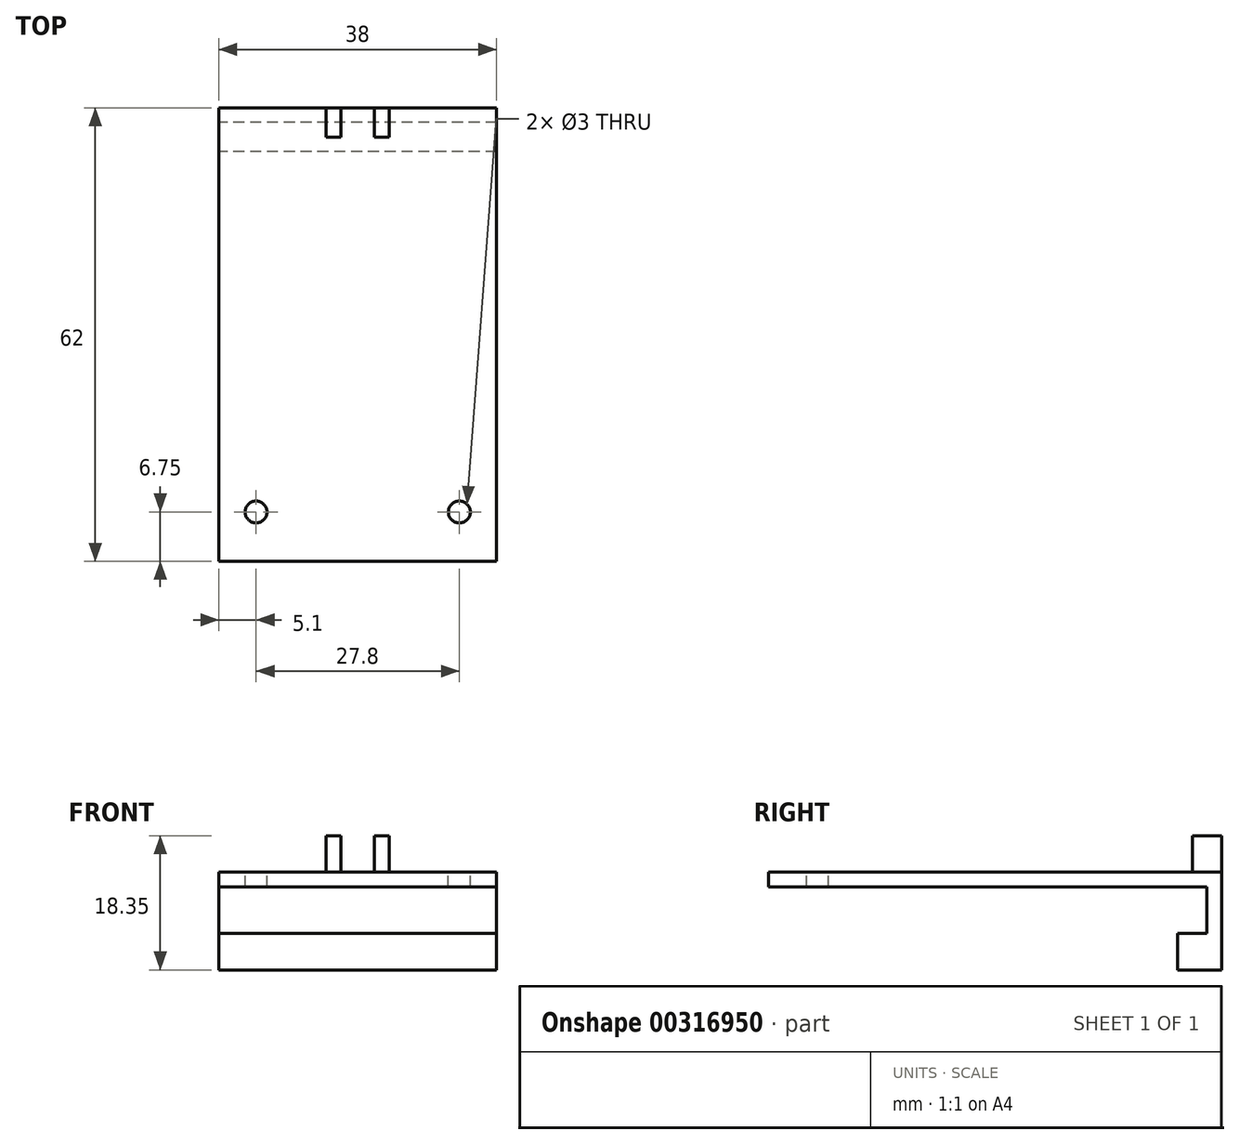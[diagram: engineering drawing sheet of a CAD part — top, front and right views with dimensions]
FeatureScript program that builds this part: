
annotation { "Feature Type Name" : "Feature", "Feature Type Description" : "" }
export const myFeature = defineFeature(function(context is Context, id is Id, definition is map)
    precondition{}
    {
        {
            var Q0;
            Q0=qCreatedBy(makeId("Top.planeOp"),FACE);
            var sketch = newSketch(context, id + "F0", { "sketchPlane" : qUnion([Q0])});
            skLineSegment(sketch, "E0.bottom", {"start": v(19, -30) * mm, "end": v(-19, -30) * mm});
            skLineSegment(sketch, "E0.top", {"start": v(19, 30) * mm, "end": v(-19, 30) * mm});
            skLineSegment(sketch, "E0.left", {"start": v(19, -30) * mm, "end": v(19, 30) * mm});
            skLineSegment(sketch, "E0.right", {"start": v(-19, -30) * mm, "end": v(-19, 30) * mm});
            skPoint(sketch, "E0.middle", {"position": v(0, 0) * mm});
            skSolve(sketch);
        }
        {
            var Q0;
            Q0=makeQuery(id+"F0.imprint","IMPRINT",FACE,{"disambiguationData":[TD([[makeQuery(id+"F0.imprint","IMPRINT",EDGE,{"derivedFrom":sQuery(id+"F0.wireOp",EDGE,"E0.bottom")}),-1.0]])]});
            extrude(context, id + "F1", {"entities" : qUnion([Q0]), "depth" : 2 * mm});
        }
        {
            var Q0;
            Q0=makeQuery(id+"F1.opExtrude","SWEPT_FACE",FACE,{"disambiguationData":[OSD([sQuery(id+"F0.wireOp",EDGE,"E0.top")])]});
            var sketch = newSketch(context, id + "F2", { "sketchPlane" : qUnion([Q0])});
            skLineSegment(sketch, "E1.bottom", {"start": v(-19, 2) * mm, "end": v(19, 2) * mm});
            skLineSegment(sketch, "E1.top", {"start": v(-19, -6.35) * mm, "end": v(19, -6.35) * mm});
            skLineSegment(sketch, "E1.left", {"start": v(-19, 2) * mm, "end": v(-19, -6.35) * mm});
            skLineSegment(sketch, "E1.right", {"start": v(19, 2) * mm, "end": v(19, -6.35) * mm});
            skSolve(sketch);
        }
        {
            var Q0;
            {var subQ0=sQuery(id+"F2.wireOp",EDGE,"E1.bottom");Q0=makeQuery(id+"F2.imprint","IMPRINT",FACE,{"disambiguationData":[TD([[makeQuery(id+"F2.imprint","IMPRINT",EDGE,{"derivedFrom":subQ0}),-1.0]])]});}
            var Q1;
            {var subQ0=sQuery(id+"F2.wireOp",EDGE,"E1.top");Q1=makeQuery(id+"F2.imprint","IMPRINT",FACE,{"disambiguationData":[TD([[makeQuery(id+"F2.imprint","IMPRINT",EDGE,{"derivedFrom":subQ0}),1.0]])]});}
            extrude(context, id + "F3", {"entities" : qUnion([Q0, Q1]), "operationType" : NewBodyOperationType.ADD, "depth" : 2 * mm});
        }
        {
            var Q0;
            Q0=makeQuery(id+"F3.opExtrude","SWEPT_FACE",FACE,{"disambiguationData":[OSD([sQuery(id+"F2.wireOp",EDGE,"E1.top")])]});
            var sketch = newSketch(context, id + "F4", { "sketchPlane" : qUnion([Q0])});
            skLineSegment(sketch, "E2.bottom", {"start": v(19, -32) * mm, "end": v(-19, -32) * mm});
            skLineSegment(sketch, "E2.top", {"start": v(19, -26) * mm, "end": v(-19, -26) * mm});
            skLineSegment(sketch, "E2.left", {"start": v(19, -32) * mm, "end": v(19, -26) * mm});
            skLineSegment(sketch, "E2.right", {"start": v(-19, -32) * mm, "end": v(-19, -26) * mm});
            skSolve(sketch);
        }
        {
            var Q0;
            Q0 = qSketchRegion(id + "F4", true);
            extrude(context, id + "F5", {"entities" : qUnion([Q0]), "operationType" : NewBodyOperationType.ADD, "depth" : 5 * mm});
        }
        {
            var Q0;
            Q0=makeQuery(id+"F3.boolean.opBoolean","MERGE",FACE,{"derivedFrom":[makeQuery(id+"F1.opExtrude","CAP_FACE",FACE,{"disambiguationData":[OSD([sQuery(id+"F0.wireOp",EDGE,"E0.bottom"),sQuery(id+"F0.wireOp",EDGE,"E0.top"),sQuery(id+"F0.wireOp",EDGE,"E0.left"),sQuery(id+"F0.wireOp",EDGE,"E0.right")])],"isStart":false}),makeQuery(id+"F3.opExtrude","SWEPT_FACE",FACE,{"disambiguationData":[OSD([sQuery(id+"F2.wireOp",EDGE,"E1.bottom")])]})]});
            var sketch = newSketch(context, id + "F6", { "sketchPlane" : qUnion([Q0])});
            skLineSegment(sketch, "E3", {"start": v(0, 32) * mm, "end": v(0, 28) * mm, "construction": true});
            skLineSegment(sketch, "E4", {"start": v(0, 32) * mm, "end": v(-2.3, 32) * mm, "construction": true});
            skLineSegment(sketch, "E5", {"start": v(-2.3, 32) * mm, "end": v(-2.3, 28) * mm, "construction": true});
            skLineSegment(sketch, "E6", {"start": v(-2.3, 28) * mm, "end": v(0, 28) * mm, "construction": true});
            skLineSegment(sketch, "E7", {"start": v(2.3, 28) * mm, "end": v(2.3, 32) * mm, "construction": true});
            skLineSegment(sketch, "E8", {"start": v(2.3, 32) * mm, "end": v(0, 32) * mm, "construction": true});
            skLineSegment(sketch, "E9", {"start": v(0, 28) * mm, "end": v(2.3, 28) * mm, "construction": true});
            skLineSegment(sketch, "E10.bottom", {"start": v(-2.3, 32) * mm, "end": v(-4.3, 32) * mm});
            skLineSegment(sketch, "E10.top", {"start": v(-2.3, 28) * mm, "end": v(-4.3, 28) * mm});
            skLineSegment(sketch, "E10.left", {"start": v(-2.3, 32) * mm, "end": v(-2.3, 28) * mm});
            skLineSegment(sketch, "E10.right", {"start": v(-4.3, 32) * mm, "end": v(-4.3, 28) * mm});
            skLineSegment(sketch, "E11.bottom", {"start": v(2.3, 28) * mm, "end": v(4.3, 28) * mm});
            skLineSegment(sketch, "E11.top", {"start": v(2.3, 32) * mm, "end": v(4.3, 32) * mm});
            skLineSegment(sketch, "E11.left", {"start": v(2.3, 28) * mm, "end": v(2.3, 32) * mm});
            skLineSegment(sketch, "E11.right", {"start": v(4.3, 28) * mm, "end": v(4.3, 32) * mm});
            skSolve(sketch);
        }
        {
            var Q0;
            Q0=makeQuery(id+"F6.imprint","IMPRINT",FACE,{"disambiguationData":[TD([[makeQuery(id+"F6.imprint","IMPRINT",EDGE,{"derivedFrom":sQuery(id+"F6.wireOp",EDGE,"E10.bottom")}),1.0]])]});
            var Q1;
            Q1=makeQuery(id+"F6.imprint","IMPRINT",FACE,{"disambiguationData":[TD([[makeQuery(id+"F6.imprint","IMPRINT",EDGE,{"derivedFrom":sQuery(id+"F6.wireOp",EDGE,"E11.bottom")}),1.0]])]});
            extrude(context, id + "F7", {"entities" : qUnion([Q0, Q1]), "operationType" : NewBodyOperationType.ADD, "depth" : 5 * mm});
        }
        {
            var Q0;
            Q0=makeQuery(id+"F3.boolean.opBoolean","MERGE",FACE,{"derivedFrom":[makeQuery(id+"F1.opExtrude","CAP_FACE",FACE,{"disambiguationData":[OSD([sQuery(id+"F0.wireOp",EDGE,"E0.bottom"),sQuery(id+"F0.wireOp",EDGE,"E0.top"),sQuery(id+"F0.wireOp",EDGE,"E0.left"),sQuery(id+"F0.wireOp",EDGE,"E0.right")])],"isStart":false}),makeQuery(id+"F3.opExtrude","SWEPT_FACE",FACE,{"disambiguationData":[OSD([sQuery(id+"F2.wireOp",EDGE,"E1.bottom")])]})]});
            var sketch = newSketch(context, id + "F8", { "sketchPlane" : qUnion([Q0])});
            skLineSegment(sketch, "E12", {"start": v(0, -23.25) * mm, "end": v(13.9, -23.25) * mm, "construction": true});
            skLineSegment(sketch, "E13", {"start": v(0, -23.25) * mm, "end": v(-13.9, -23.25) * mm, "construction": true});
            skCircle(sketch, "E14", {"center": v(-13.9, -23.25) * mm, "radius": 1.5 * mm});
            skCircle(sketch, "E15", {"center": v(13.9, -23.25) * mm, "radius": 1.5 * mm});
            skSolve(sketch);
        }
        {
            var Q0;
            Q0 = qSketchRegion(id + "F8", true);
            extrude(context, id + "F9", {"entities" : qUnion([Q0]), "operationType" : NewBodyOperationType.REMOVE, "oppositeDirection" : true, "depth" : 25 * mm});
        }
    });
